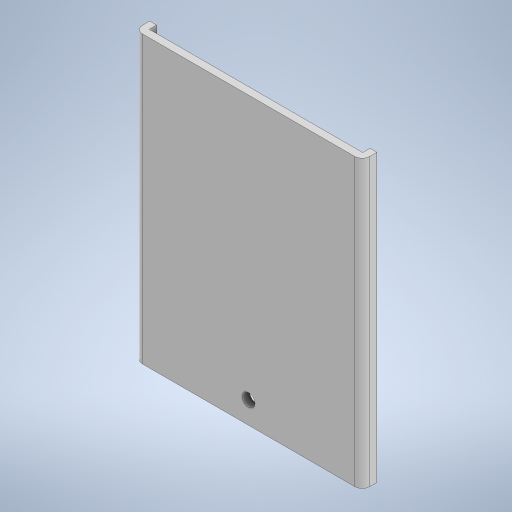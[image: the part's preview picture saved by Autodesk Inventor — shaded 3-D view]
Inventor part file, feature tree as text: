
AUTODESK INVENTOR PART (.ipt)
format: ipt  version: 2023.1 (Build 271208000, 208)  size: 226,816 bytes
history: native  units: mm
features: extrude x3, sketch x2, other x1, fillet x1
ambient origin geometry x8: Origin, YZ Plane, XZ Plane, XY Plane, X Axis, Y Axis, Z Axis, Center Point
bodies: Body1 (feature_tree)
feature tree (7):
  other  "솔리드1"
  sketch  "스케치1"
  extrude  "돌출1"  Depth=62.0mm
  extrude  "돌출2"  Depth=78.0mm
  sketch  "스케치2"
  extrude  "돌출4"  Depth=1.9mm
  fillet  "모깎기1"  Radius=2.0mm
